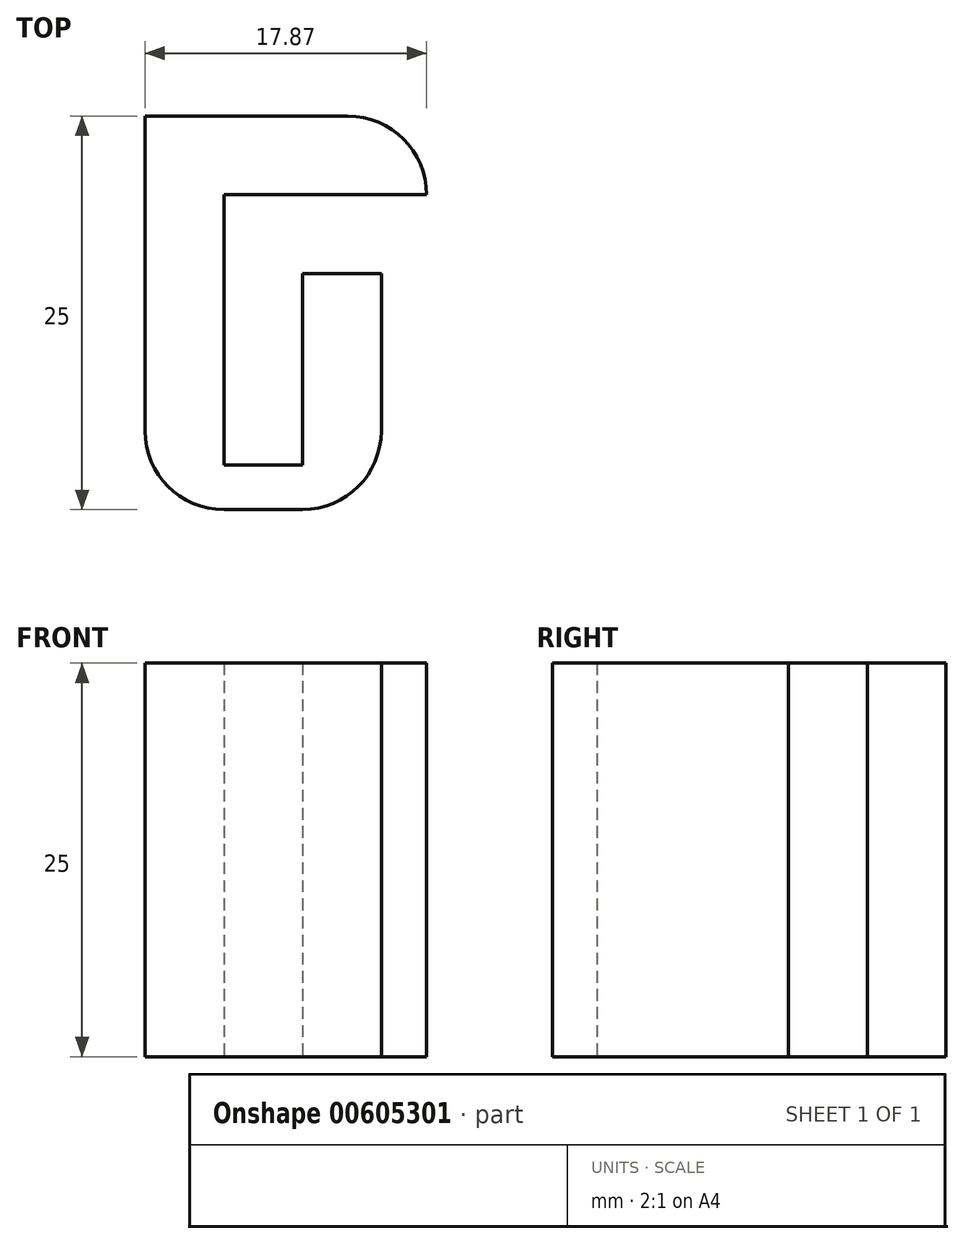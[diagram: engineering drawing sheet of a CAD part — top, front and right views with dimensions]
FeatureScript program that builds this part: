
annotation { "Feature Type Name" : "Feature", "Feature Type Description" : "" }
export const myFeature = defineFeature(function(context is Context, id is Id, definition is map)
    precondition{}
    {
        {
            var Q0;
            Q0=qCreatedBy(makeId("Top.planeOp"),FACE);
            var sketch = newSketch(context, id + "F0", { "sketchPlane" : qUnion([Q0])});
            skLineSegment(sketch, "E0.bottom", {"start": v(0, 0) * mm, "end": v(17.87, 0) * mm});
            skLineSegment(sketch, "E0.top", {"start": v(0, -5) * mm, "end": v(17.87, -5) * mm});
            skLineSegment(sketch, "E0.left", {"start": v(0, -5) * mm, "end": v(0, 0) * mm});
            skLineSegment(sketch, "E0.right", {"start": v(17.87, -5) * mm, "end": v(17.87, 0) * mm});
            skLineSegment(sketch, "E1.bottom", {"start": v(0, 0) * mm, "end": v(5, 0) * mm});
            skLineSegment(sketch, "E1.top", {"start": v(0, -25) * mm, "end": v(5, -25) * mm});
            skLineSegment(sketch, "E1.left", {"start": v(0, 0) * mm, "end": v(0, -25) * mm});
            skLineSegment(sketch, "E1.right", {"start": v(5, 0) * mm, "end": v(5, -25) * mm});
            skLineSegment(sketch, "E2.bottom", {"start": v(5, -25) * mm, "end": v(10, -25) * mm});
            skLineSegment(sketch, "E2.top", {"start": v(5, -22.17) * mm, "end": v(10, -22.17) * mm});
            skLineSegment(sketch, "E2.left", {"start": v(5, -25) * mm, "end": v(5, -22.17) * mm});
            skLineSegment(sketch, "E2.right", {"start": v(10, -25) * mm, "end": v(10, -22.17) * mm});
            skLineSegment(sketch, "E3.bottom", {"start": v(10, -25) * mm, "end": v(15, -25) * mm});
            skLineSegment(sketch, "E3.top", {"start": v(10, -10) * mm, "end": v(15, -10) * mm});
            skLineSegment(sketch, "E3.left", {"start": v(10, -25) * mm, "end": v(10, -10) * mm});
            skLineSegment(sketch, "E3.right", {"start": v(15, -25) * mm, "end": v(15, -10) * mm});
            skSolve(sketch);
        }
        {
            var Q0;
            Q0 = qSketchRegion(id + "F0", true);
            extrude(context, id + "F1", {"entities" : qUnion([Q0]), "depth" : 25 * mm, "offsetDistance" : 25 * mm});
        }
        {
            var Q0;
            Q0=makeQuery(id+"F1.opExtrude","SWEPT_EDGE",EDGE,{"disambiguationData":[OSD([sQuery(id+"F0.wireOp",EDGE,"E1.bottom"),sQuery(id+"F0.wireOp",EDGE,"E1.left")])]});
            var Q1;
            Q1=makeQuery(id+"F1.opExtrude","SWEPT_EDGE",EDGE,{"disambiguationData":[OSD([sQuery(id+"F0.wireOp",EDGE,"E1.top"),sQuery(id+"F0.wireOp",EDGE,"E1.left")])]});
            var Q2;
            Q2=makeQuery(id+"F1.opExtrude","SWEPT_EDGE",EDGE,{"disambiguationData":[OSD([sQuery(id+"F0.wireOp",EDGE,"E3.bottom"),sQuery(id+"F0.wireOp",EDGE,"E3.right")])]});
            var Q3;
            Q3=makeQuery(id+"F1.opExtrude","SWEPT_EDGE",EDGE,{"disambiguationData":[OSD([sQuery(id+"F0.wireOp",EDGE,"E0.bottom"),sQuery(id+"F0.wireOp",EDGE,"E0.right")])]});
            fillet(context, id + "F2", {"entities" : qUnion([Q0, Q1, Q2, Q3]), "radius" : 5 * mm, "tangentPropagation" : true, "allowEdgeOverflow" : false});
        }
    });
